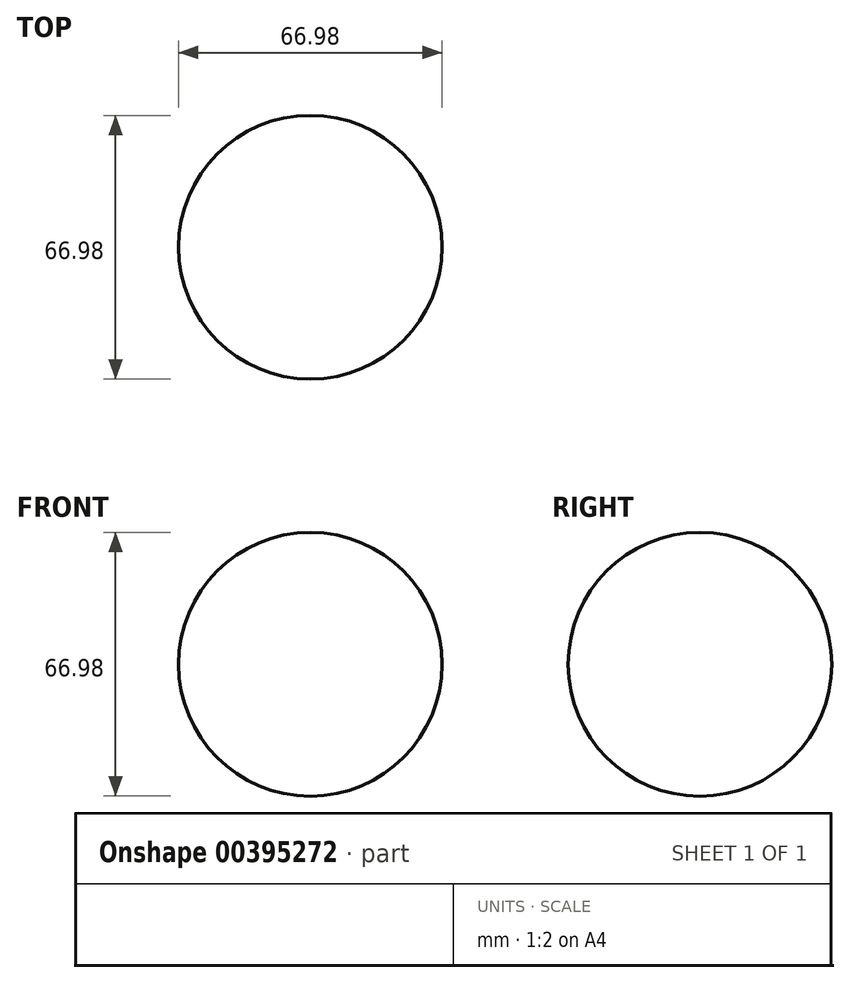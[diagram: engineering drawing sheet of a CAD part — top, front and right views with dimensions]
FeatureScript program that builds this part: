
annotation { "Feature Type Name" : "Feature", "Feature Type Description" : "" }
export const myFeature = defineFeature(function(context is Context, id is Id, definition is map)
    precondition{}
    {
        {
            var Q0;
            Q0=qCreatedBy(makeId("Front.planeOp"),FACE);
            var sketch = newSketch(context, id + "F0", { "sketchPlane" : qUnion([Q0])});
            skArc(sketch, "E0", {"start": v(0, -33.5) * mm, "mid": v(33.5, 0) * mm, "end": v(0, 33.5) * mm});
            skLineSegment(sketch, "E1", {"start": v(0, 33.5) * mm, "end": v(0, -33.5) * mm});
            skSolve(sketch);
        }
        {
            var Q0;
            Q0=qCreatedBy(makeId("Front.planeOp"),FACE);
            var sketch = newSketch(context, id + "F1", { "sketchPlane" : qUnion([Q0])});
            skLineSegment(sketch, "E2", {"start": v(0, 0) * mm, "end": v(0, 43.17) * mm, "construction": true});
            skSolve(sketch);
        }
        {
            var Q0;
            Q0 = qSketchRegion(id + "F0", true);
            var Q1;
            Q1=sQuery(id+"F1.wireOp",EDGE,"E2");
            revolve(context, id + "F2", {"entities" : qUnion([Q0]), "axis" : qUnion([Q1]), "revolveType" : RevolveType.FULL});
        }
    });
